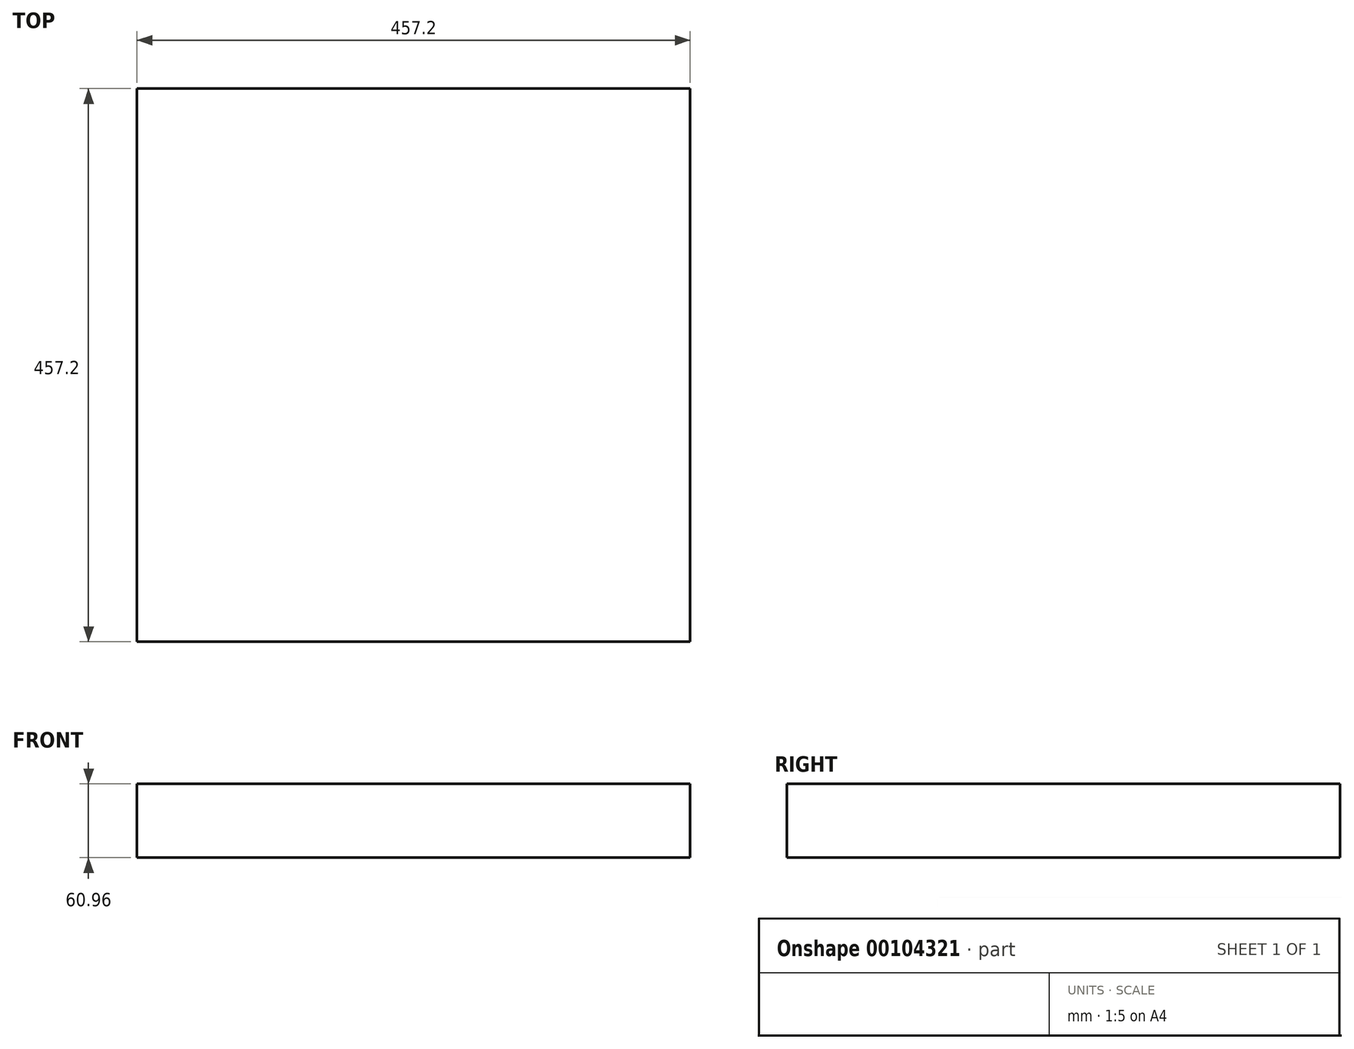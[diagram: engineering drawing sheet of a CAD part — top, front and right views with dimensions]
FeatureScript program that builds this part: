
annotation { "Feature Type Name" : "Feature", "Feature Type Description" : "" }
export const myFeature = defineFeature(function(context is Context, id is Id, definition is map)
    precondition{}
    {
        {
            var Q0;
            Q0=qCreatedBy(makeId("Top.planeOp"),FACE);
            var sketch = newSketch(context, id + "F0", { "sketchPlane" : qUnion([Q0])});
            skLineSegment(sketch, "E0.bottom", {"start": v(-228.6, 228.6) * mm, "end": v(228.6, 228.6) * mm});
            skLineSegment(sketch, "E0.top", {"start": v(-228.6, -228.6) * mm, "end": v(228.6, -228.6) * mm});
            skLineSegment(sketch, "E0.left", {"start": v(-228.6, 228.6) * mm, "end": v(-228.6, -228.6) * mm});
            skLineSegment(sketch, "E0.right", {"start": v(228.6, 228.6) * mm, "end": v(228.6, -228.6) * mm});
            skPoint(sketch, "E0.middle", {"position": v(0, 0) * mm});
            skSolve(sketch);
        }
        {
            var Q0;
            Q0 = qSketchRegion(id + "F0", true);
            extrude(context, id + "F1", {"entities" : qUnion([Q0]), "depth" : 60.96 * mm});
        }
    });
